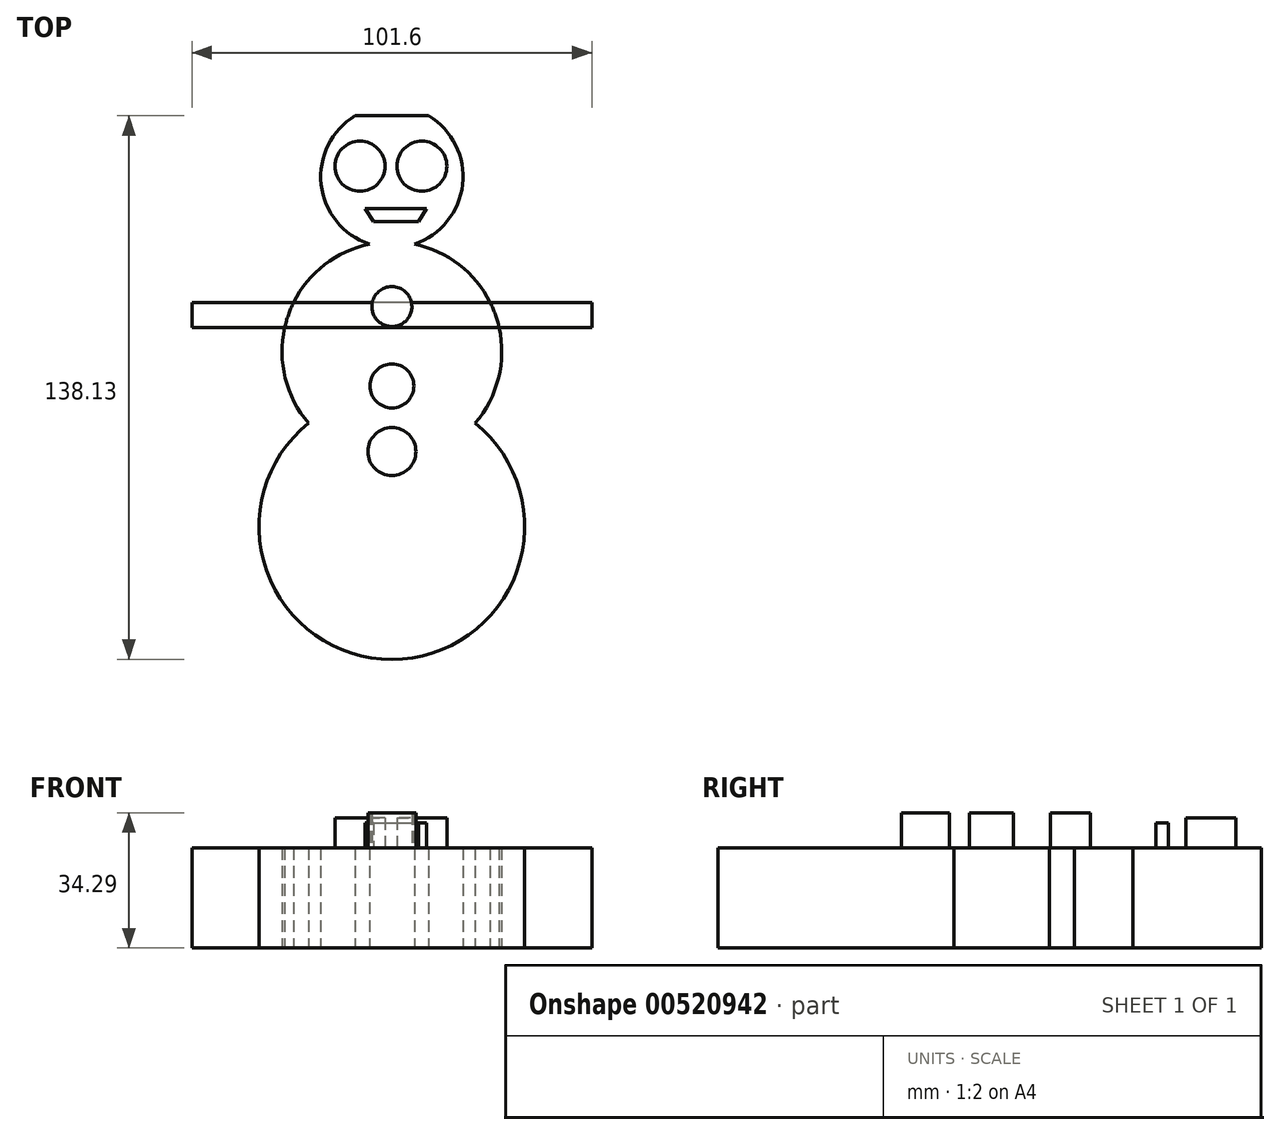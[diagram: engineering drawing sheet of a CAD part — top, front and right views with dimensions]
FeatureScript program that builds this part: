
annotation { "Feature Type Name" : "Feature", "Feature Type Description" : "" }
export const myFeature = defineFeature(function(context is Context, id is Id, definition is map)
    precondition{}
    {
        {
            var Q0;
            Q0=qCreatedBy(makeId("Top.planeOp"),FACE);
            var sketch = newSketch(context, id + "F0", { "sketchPlane" : qUnion([Q0])});
            skCircle(sketch, "E0", {"center": v(0, -44.45) * mm, "radius": 33.75 * mm});
            skCircle(sketch, "E1", {"center": v(0, 0) * mm, "radius": 27.9 * mm});
            skCircle(sketch, "E2", {"center": v(0, 44.45) * mm, "radius": 18.07 * mm});
            skLineSegment(sketch, "E3.bottom", {"start": v(0, 12.45) * mm, "end": v(50.8, 12.45) * mm});
            skLineSegment(sketch, "E3.top", {"start": v(0, 6.1) * mm, "end": v(50.8, 6.1) * mm});
            skLineSegment(sketch, "E3.left", {"start": v(0, 12.45) * mm, "end": v(0, 6.1) * mm});
            skLineSegment(sketch, "E3.right", {"start": v(50.8, 12.45) * mm, "end": v(50.8, 6.1) * mm});
            skLineSegment(sketch, "E4.bottom", {"start": v(0, 6.1) * mm, "end": v(-50.8, 6.1) * mm});
            skLineSegment(sketch, "E4.top", {"start": v(0, 12.45) * mm, "end": v(-50.8, 12.45) * mm});
            skLineSegment(sketch, "E4.left", {"start": v(0, 6.1) * mm, "end": v(0, 12.45) * mm});
            skLineSegment(sketch, "E4.right", {"start": v(-50.8, 6.1) * mm, "end": v(-50.8, 12.45) * mm});
            skLineSegment(sketch, "E5.bottom", {"start": v(19.57, 59.93) * mm, "end": v(-19, 59.93) * mm});
            skLineSegment(sketch, "E5.top", {"start": v(19.57, 64.13) * mm, "end": v(-19, 64.13) * mm});
            skLineSegment(sketch, "E5.left", {"start": v(19.57, 59.93) * mm, "end": v(19.57, 64.13) * mm});
            skLineSegment(sketch, "E5.right", {"start": v(-19, 59.93) * mm, "end": v(-19, 64.13) * mm});
            skLineSegment(sketch, "E6.bottom", {"start": v(-10.9, 64.13) * mm, "end": v(6.99, 64.13) * mm});
            skLineSegment(sketch, "E6.top", {"start": v(-10.9, 76.43) * mm, "end": v(6.99, 76.43) * mm});
            skLineSegment(sketch, "E6.left", {"start": v(-10.9, 64.13) * mm, "end": v(-10.9, 76.43) * mm});
            skLineSegment(sketch, "E6.right", {"start": v(6.99, 64.13) * mm, "end": v(6.99, 76.43) * mm});
            skSolve(sketch);
        }
        {
            var Q0;
            {var subQ0=sQuery(id+"F0.wireOp",EDGE,"E2");var subQ1=sQuery(id+"F0.wireOp",EDGE,"E1");var subQ2=makeQuery(id+"F0.imprint","INTERSECT",VERTEX,{"disambiguationData":[OD(0.0)],"derivedFrom":[subQ1,subQ0]});Q0=makeQuery(id+"F0.imprint","IMPRINT",FACE,{"disambiguationData":[TD([[makeQuery(id+"F0.imprint","IMPRINT",EDGE,{"disambiguationData":[TD([[subQ2,1.0]])],"derivedFrom":subQ1}),-1.0]])]});}
            var Q1;
            {var subQ0=sQuery(id+"F0.wireOp",EDGE,"E1");var subQ1=sQuery(id+"F0.wireOp",EDGE,"E0");var subQ2=makeQuery(id+"F0.imprint","INTERSECT",VERTEX,{"disambiguationData":[OD(0.0)],"derivedFrom":[subQ1,subQ0]});Q1=makeQuery(id+"F0.imprint","IMPRINT",FACE,{"disambiguationData":[TD([[makeQuery(id+"F0.imprint","IMPRINT",EDGE,{"disambiguationData":[TD([[subQ2,1.0]])],"derivedFrom":subQ1}),-1.0]])]});}
            var Q2;
            {var subQ0=sQuery(id+"F0.wireOp",EDGE,"E1");var subQ1=sQuery(id+"F0.wireOp",EDGE,"E0");var subQ2=makeQuery(id+"F0.imprint","INTERSECT",VERTEX,{"disambiguationData":[OD(0.0)],"derivedFrom":[subQ1,subQ0]});Q2=makeQuery(id+"F0.imprint","IMPRINT",FACE,{"disambiguationData":[TD([[makeQuery(id+"F0.imprint","IMPRINT",EDGE,{"disambiguationData":[TD([[subQ2,-1.0]])],"derivedFrom":subQ1}),1.0]])]});}
            var Q3;
            {var subQ0=sQuery(id+"F0.wireOp",EDGE,"E1");var subQ1=sQuery(id+"F0.wireOp",EDGE,"E0");var subQ2=makeQuery(id+"F0.imprint","INTERSECT",VERTEX,{"disambiguationData":[OD(0.0)],"derivedFrom":[subQ1,subQ0]});Q3=makeQuery(id+"F0.imprint","IMPRINT",FACE,{"disambiguationData":[TD([[makeQuery(id+"F0.imprint","IMPRINT",EDGE,{"disambiguationData":[TD([[subQ2,1.0]])],"derivedFrom":subQ1}),1.0]])]});}
            var Q4;
            {var subQ0=sQuery(id+"F0.wireOp",EDGE,"E2");var subQ1=sQuery(id+"F0.wireOp",EDGE,"E1");var subQ2=makeQuery(id+"F0.imprint","INTERSECT",VERTEX,{"disambiguationData":[OD(0.0)],"derivedFrom":[subQ1,subQ0]});Q4=makeQuery(id+"F0.imprint","IMPRINT",FACE,{"disambiguationData":[TD([[makeQuery(id+"F0.imprint","IMPRINT",EDGE,{"disambiguationData":[TD([[subQ2,1.0]])],"derivedFrom":subQ1}),1.0]])]});}
            var Q5;
            {var subQ5=sQuery(id+"F0.wireOp",EDGE,"E4.right");Q5=makeQuery(id+"F0.imprint","IMPRINT",FACE,{"disambiguationData":[TD([[makeQuery(id+"F0.imprint","IMPRINT",EDGE,{"derivedFrom":subQ5}),-1.0]])]});}
            var Q6;
            {var subQ5=sQuery(id+"F0.wireOp",EDGE,"E3.right");Q6=makeQuery(id+"F0.imprint","IMPRINT",FACE,{"disambiguationData":[TD([[makeQuery(id+"F0.imprint","IMPRINT",EDGE,{"derivedFrom":subQ5}),-1.0]])]});}
            var Q7;
            {var subQ5=sQuery(id+"F0.wireOp",EDGE,"E4.left");Q7=makeQuery(id+"F0.imprint","IMPRINT",FACE,{"disambiguationData":[TD([[makeQuery(id+"F0.imprint","IMPRINT",EDGE,{"derivedFrom":subQ5}),-1.0]])]});}
            var Q8;
            {var subQ5=sQuery(id+"F0.wireOp",EDGE,"E4.left");Q8=makeQuery(id+"F0.imprint","IMPRINT",FACE,{"disambiguationData":[TD([[makeQuery(id+"F0.imprint","IMPRINT",EDGE,{"derivedFrom":subQ5}),1.0]])]});}
            var Q9;
            {var subQ0=sQuery(id+"F0.wireOp",EDGE,"E2");var subQ1=sQuery(id+"F0.wireOp",EDGE,"E1");var subQ2=makeQuery(id+"F0.imprint","INTERSECT",VERTEX,{"disambiguationData":[OD(0.0)],"derivedFrom":[subQ1,subQ0]});Q9=makeQuery(id+"F0.imprint","IMPRINT",FACE,{"disambiguationData":[TD([[makeQuery(id+"F0.imprint","IMPRINT",EDGE,{"disambiguationData":[TD([[subQ2,-1.0]])],"derivedFrom":subQ1}),1.0]])]});}
            var Q10;
            {var subQ0=sQuery(id+"F0.wireOp",EDGE,"E2");var subQ1=sQuery(id+"F0.wireOp",EDGE,"E1");var subQ2=makeQuery(id+"F0.imprint","INTERSECT",VERTEX,{"disambiguationData":[OD(0.0)],"derivedFrom":[subQ1,subQ0]});Q10=makeQuery(id+"F0.imprint","IMPRINT",FACE,{"disambiguationData":[TD([[makeQuery(id+"F0.imprint","IMPRINT",EDGE,{"disambiguationData":[TD([[subQ2,-1.0]])],"derivedFrom":subQ1}),-1.0]])]});}
            extrude(context, id + "F1", {"entities" : qUnion([Q0, Q1, Q2, Q3, Q4, Q5, Q6, Q7, Q8, Q9, Q10]), "depth" : 25.4 * mm, "offsetDistance" : 25.4 * mm});
        }
        {
            var Q0;
            Q0=makeQuery(id+"F1.opExtrude","CAP_FACE",FACE,{"disambiguationData":[OSD([sQuery(id+"F0.wireOp",EDGE,"E0"),sQuery(id+"F0.wireOp",EDGE,"E1"),sQuery(id+"F0.wireOp",EDGE,"E2")])],"isStart":false});
            var sketch = newSketch(context, id + "F2", { "sketchPlane" : qUnion([Q0])});
            skCircle(sketch, "E7", {"center": v(-8.1, 47.1) * mm, "radius": 6.35 * mm});
            skCircle(sketch, "E8", {"center": v(7.62, 47.1) * mm, "radius": 6.35 * mm});
            skSolve(sketch);
        }
        {
            var Q0;
            Q0=makeQuery(id+"F2.imprint","IMPRINT",FACE,{"disambiguationData":[TD([[makeQuery(id+"F2.imprint","IMPRINT",EDGE,{"derivedFrom":sQuery(id+"F2.wireOp",EDGE,"E7")}),1.0]])]});
            var Q1;
            Q1=makeQuery(id+"F2.imprint","IMPRINT",FACE,{"disambiguationData":[TD([[makeQuery(id+"F2.imprint","IMPRINT",EDGE,{"derivedFrom":sQuery(id+"F2.wireOp",EDGE,"E8")}),1.0]])]});
            extrude(context, id + "F3", {"entities" : qUnion([Q0, Q1]), "operationType" : NewBodyOperationType.ADD, "depth" : 7.62 * mm, "offsetDistance" : 25.4 * mm});
        }
        {
            var Q0;
            Q0=makeQuery(id+"F1.opExtrude","CAP_FACE",FACE,{"disambiguationData":[OSD([sQuery(id+"F0.wireOp",EDGE,"E0"),sQuery(id+"F0.wireOp",EDGE,"E1"),sQuery(id+"F0.wireOp",EDGE,"E2")])],"isStart":false});
            var sketch = newSketch(context, id + "F4", { "sketchPlane" : qUnion([Q0])});
            skCircle(sketch, "E9", {"center": v(0, 11.43) * mm, "radius": 5.08 * mm});
            skCircle(sketch, "E10", {"center": v(0, -8.73) * mm, "radius": 5.59 * mm});
            skCircle(sketch, "E11", {"center": v(0, -25.4) * mm, "radius": 6.1 * mm});
            skSolve(sketch);
        }
        {
            var Q0;
            Q0=makeQuery(id+"F4.imprint","IMPRINT",FACE,{"disambiguationData":[TD([[makeQuery(id+"F4.imprint","IMPRINT",EDGE,{"derivedFrom":sQuery(id+"F4.wireOp",EDGE,"E9")}),1.0]])]});
            var Q1;
            Q1=makeQuery(id+"F4.imprint","IMPRINT",FACE,{"disambiguationData":[TD([[makeQuery(id+"F4.imprint","IMPRINT",EDGE,{"derivedFrom":sQuery(id+"F4.wireOp",EDGE,"E10")}),1.0]])]});
            var Q2;
            Q2=makeQuery(id+"F4.imprint","IMPRINT",FACE,{"disambiguationData":[TD([[makeQuery(id+"F4.imprint","IMPRINT",EDGE,{"derivedFrom":sQuery(id+"F4.wireOp",EDGE,"E11")}),1.0]])]});
            extrude(context, id + "F5", {"entities" : qUnion([Q0, Q1, Q2]), "operationType" : NewBodyOperationType.ADD, "depth" : 8.9 * mm, "offsetDistance" : 25.4 * mm});
        }
        {
            var Q0;
            Q0=makeQuery(id+"F1.opExtrude","CAP_FACE",FACE,{"disambiguationData":[OSD([sQuery(id+"F0.wireOp",EDGE,"E0"),sQuery(id+"F0.wireOp",EDGE,"E1"),sQuery(id+"F0.wireOp",EDGE,"E2"),sQuery(id+"F0.wireOp",EDGE,"E3.bottom"),sQuery(id+"F0.wireOp",EDGE,"E3.top"),sQuery(id+"F0.wireOp",EDGE,"E3.right"),sQuery(id+"F0.wireOp",EDGE,"E4.bottom"),sQuery(id+"F0.wireOp",EDGE,"E4.top"),sQuery(id+"F0.wireOp",EDGE,"E4.right")])],"isStart":false});
            var sketch = newSketch(context, id + "F6", { "sketchPlane" : qUnion([Q0])});
            skLineSegment(sketch, "E12", {"start": v(-4.7, 33.05) * mm, "end": v(6.76, 33.05) * mm});
            skLineSegment(sketch, "E13", {"start": v(-4.7, 33.05) * mm, "end": v(-6.76, 36.3) * mm});
            skLineSegment(sketch, "E14", {"start": v(-6.76, 36.3) * mm, "end": v(8.82, 36.3) * mm});
            skLineSegment(sketch, "E15", {"start": v(8.82, 36.3) * mm, "end": v(6.76, 33.05) * mm});
            skSolve(sketch);
        }
        {
            var Q0;
            Q0=makeQuery(id+"F6.imprint","IMPRINT",FACE,{"disambiguationData":[TD([[makeQuery(id+"F6.imprint","IMPRINT",EDGE,{"derivedFrom":sQuery(id+"F6.wireOp",EDGE,"E12")}),1.0]])]});
            extrude(context, id + "F7", {"entities" : qUnion([Q0]), "operationType" : NewBodyOperationType.ADD, "depth" : 6.35 * mm, "offsetDistance" : 25.4 * mm});
        }
    });
